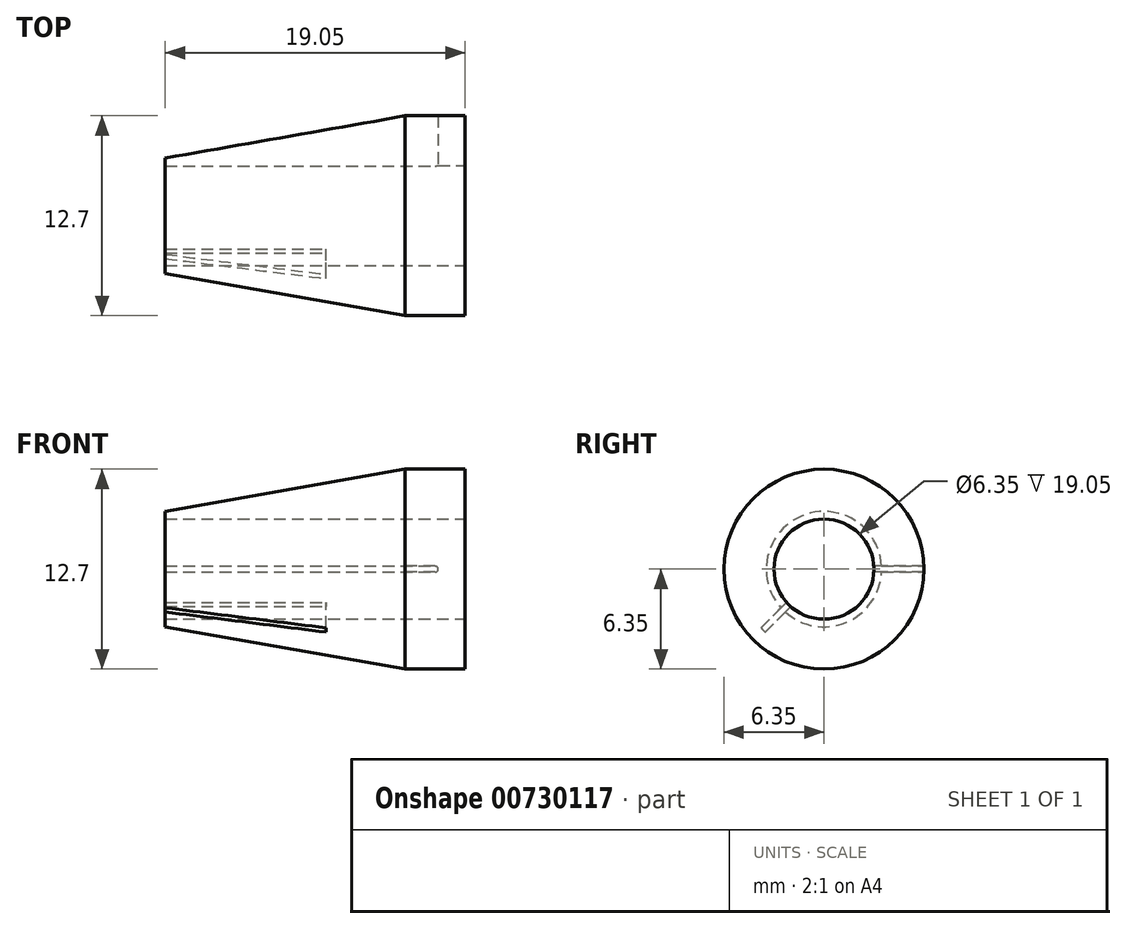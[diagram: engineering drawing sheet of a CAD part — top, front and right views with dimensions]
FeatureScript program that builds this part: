
annotation { "Feature Type Name" : "Feature", "Feature Type Description" : "" }
export const myFeature = defineFeature(function(context is Context, id is Id, definition is map)
    precondition{}
    {
        {
            var Q0;
            Q0=qCreatedBy(makeId("Top.planeOp"),FACE);
            var sketch = newSketch(context, id + "F0", { "sketchPlane" : qUnion([Q0])});
            skLineSegment(sketch, "E0", {"start": v(0, 0) * mm, "end": v(19.05, 0) * mm});
            skLineSegment(sketch, "E1", {"start": v(19.05, 0) * mm, "end": v(19.05, 6.35) * mm});
            skLineSegment(sketch, "E2", {"start": v(19.05, 6.35) * mm, "end": v(15.24, 6.35) * mm});
            skLineSegment(sketch, "E3", {"start": v(15.24, 6.35) * mm, "end": v(0, 3.66) * mm});
            skLineSegment(sketch, "E4", {"start": v(0, 3.66) * mm, "end": v(0, 0) * mm});
            skSolve(sketch);
        }
        {
            var Q0;
            Q0 = qSketchRegion(id + "F0", true);
            var Q1;
            Q1=sQuery(id+"F0.wireOp",EDGE,"E0");
            revolve(context, id + "F1", {"surfaceOperationType" : NewSurfaceOperationType.NEW, "entities" : qUnion([Q0]), "axis" : qUnion([Q1]), "revolveType" : RevolveType.FULL});
        }
        {
            var Q0;
            Q0=makeQuery(id+"F1.opRevolve","SWEPT_FACE",FACE,{"disambiguationData":[OSD([sQuery(id+"F0.wireOp",EDGE,"E1")])]});
            var sketch = newSketch(context, id + "F2", { "sketchPlane" : qUnion([Q0])});
            skCircle(sketch, "E5", {"center": v(0, 0) * mm, "radius": 3.18 * mm});
            skSolve(sketch);
        }
        {
            var Q0;
            Q0 = qSketchRegion(id + "F2", true);
            extrude(context, id + "F3", {"entities" : qUnion([Q0]), "operationType" : NewBodyOperationType.REMOVE, "endBound" : BoundingType.THROUGH_ALL, "oppositeDirection" : true, "depth" : 25.4 * mm, "offsetDistance" : 25.4 * mm});
        }
        {
            var Q0;
            Q0=qCreatedBy(makeId("Front.planeOp"),FACE);
            var sketch = newSketch(context, id + "F4", { "sketchPlane" : qUnion([Q0])});
            skLineSegment(sketch, "E6.bottom", {"start": v(0, -0.2) * mm, "end": v(17.14, -0.2) * mm});
            skLineSegment(sketch, "E6.top", {"start": v(0, 0.2) * mm, "end": v(17.14, 0.2) * mm});
            skLineSegment(sketch, "E6.left", {"start": v(0, -0.2) * mm, "end": v(0, 0.2) * mm});
            skLineSegment(sketch, "E6.right", {"start": v(17.34, 0) * mm, "end": v(17.34, 0) * mm});
            skPoint(sketch, "E7.visualSharp", {"position": v(17.34, -0.2) * mm});
            skArc(sketch, "E7.filletArc", {"start": v(17.14, -0.2) * mm, "mid": v(17.28, -0.13) * mm, "end": v(17.34, 0) * mm});
            skPoint(sketch, "E8.visualSharp", {"position": v(17.34, 0.2) * mm});
            skArc(sketch, "E8.filletArc", {"start": v(17.34, 0) * mm, "mid": v(17.28, 0.13) * mm, "end": v(17.14, 0.2) * mm});
            skSolve(sketch);
        }
        {
            var Q0;
            Q0 = qSketchRegion(id + "F4", true);
            extrude(context, id + "F5", {"entities" : qUnion([Q0]), "operationType" : NewBodyOperationType.REMOVE, "endBound" : BoundingType.THROUGH_ALL, "oppositeDirection" : true, "depth" : 25.4 * mm, "offsetDistance" : 25.4 * mm});
        }
        {
            var Q0;
            Q0=qCreatedBy(makeId("Front.planeOp"),FACE);
            var sketch = newSketch(context, id + "F6", { "sketchPlane" : qUnion([Q0])});
            skLineSegment(sketch, "E9", {"start": v(0, 0) * mm, "end": v(24.18, 0) * mm});
            skSolve(sketch);
        }
        {
            var Q0;
            Q0 = qBodyType(qCreatedBy(id + "F6" ,EDGE), BodyType.WIRE);
            var Q1;
            Q1=qCreatedBy(makeId("Front.planeOp"),FACE);
            cPlane(context, id + "F7", {"entities" : qUnion([Q0, Q1]), "cplaneType" : CPlaneType.LINE_ANGLE, "offset" : 25.4 * mm, "angle" : 45 * degree, "width" : 152.4 * mm, "height" : 152.4 * mm});
        }
        {
            var Q0;
            Q0=qCreatedBy(id+"F7.planeOp",FACE);
            var sketch = newSketch(context, id + "F8", { "sketchPlane" : qUnion([Q0])});
            skLineSegment(sketch, "E10.bottom", {"start": v(0, 0.2) * mm, "end": v(-10.21, 0.2) * mm});
            skLineSegment(sketch, "E10.top", {"start": v(0, -0.2) * mm, "end": v(-10.21, -0.2) * mm});
            skLineSegment(sketch, "E10.left", {"start": v(0, 0.2) * mm, "end": v(0, -0.2) * mm});
            skLineSegment(sketch, "E10.right", {"start": v(-10.21, 0.2) * mm, "end": v(-10.21, -0.2) * mm});
            skSolve(sketch);
        }
        {
            var Q0;
            Q0 = qSketchRegion(id + "F8", true);
            extrude(context, id + "F9", {"entities" : qUnion([Q0]), "operationType" : NewBodyOperationType.REMOVE, "endBound" : BoundingType.THROUGH_ALL, "oppositeDirection" : true, "depth" : 25.4 * mm, "offsetDistance" : 25.4 * mm});
        }
    });
